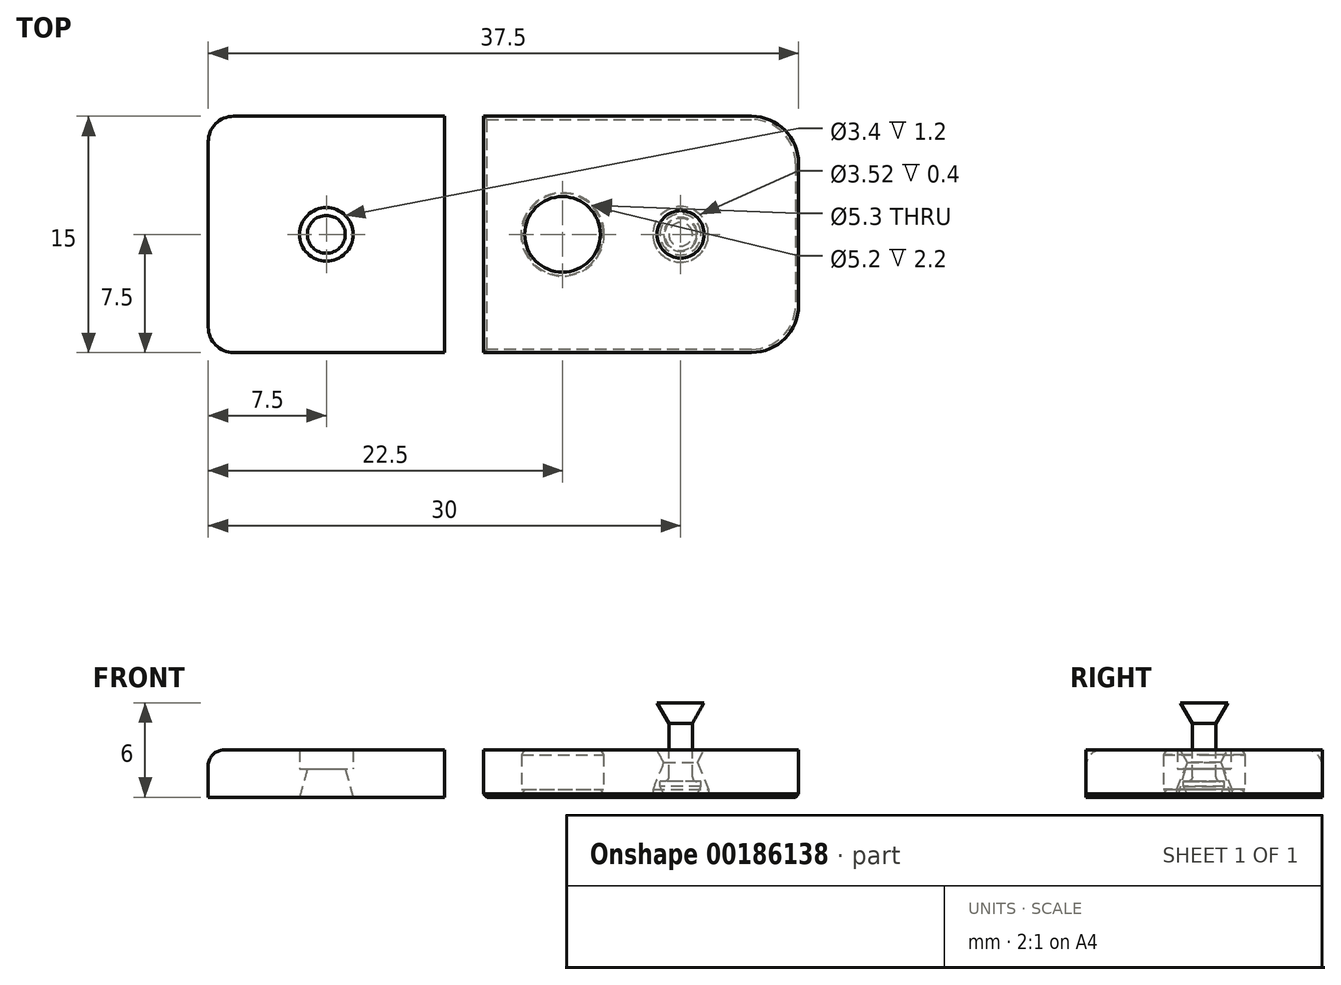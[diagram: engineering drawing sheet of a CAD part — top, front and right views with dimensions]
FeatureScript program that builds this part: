
annotation { "Feature Type Name" : "Feature", "Feature Type Description" : "" }
export const myFeature = defineFeature(function(context is Context, id is Id, definition is map)
    precondition{}
    {
        {
            var Q0;
            Q0=qCreatedBy(makeId("Top.planeOp"),FACE);
            var sketch = newSketch(context, id + "F0", { "sketchPlane" : qUnion([Q0])});
            skLineSegment(sketch, "E0.bottom", {"start": v(-12.5, 7.5) * mm, "end": v(7.5, 7.5) * mm});
            skLineSegment(sketch, "E0.top", {"start": v(-12.5, -7.5) * mm, "end": v(7.5, -7.5) * mm});
            skLineSegment(sketch, "E0.left", {"start": v(-12.5, 7.5) * mm, "end": v(-12.5, -7.5) * mm});
            skLineSegment(sketch, "E0.right", {"start": v(7.5, 7.5) * mm, "end": v(7.5, -7.5) * mm});
            skSolve(sketch);
        }
        {
            var Q0;
            Q0=makeQuery(id+"F0.imprint","IMPRINT",FACE,{"disambiguationData":[TD([[makeQuery(id+"F0.imprint","IMPRINT",EDGE,{"derivedFrom":sQuery(id+"F0.wireOp",EDGE,"E0.bottom")}),-1.0]])]});
            extrude(context, id + "F1", {"entities" : qUnion([Q0]), "depth" : 3 * mm});
        }
        {
            var Q0;
            Q0=qCreatedBy(makeId("Front.planeOp"),FACE);
            var sketch = newSketch(context, id + "F2", { "sketchPlane" : qUnion([Q0])});
            skLineSegment(sketch, "E1", {"start": v(0, 3.74) * mm, "end": v(0, -0.54) * mm, "construction": true});
            skLineSegment(sketch, "E2", {"start": v(-1.76, 0) * mm, "end": v(0, 0) * mm});
            skLineSegment(sketch, "E3", {"start": v(-1.07, 2.2) * mm, "end": v(-1.5, 3) * mm});
            skLineSegment(sketch, "E4", {"start": v(-1.5, 3) * mm, "end": v(0, 3) * mm});
            skLineSegment(sketch, "E5", {"start": v(0, 3) * mm, "end": v(0, 0) * mm});
            skLineSegment(sketch, "E6", {"start": v(-1.76, 0) * mm, "end": v(-1.76, 0.5) * mm});
            skLineSegment(sketch, "E7", {"start": v(-1.76, 0.5) * mm, "end": v(-1.07, 2.2) * mm});
            skSolve(sketch);
        }
        {
            var Q0;
            Q0 = qSketchRegion(id + "F2", true);
            var Q1;
            Q1=sQuery(id+"F2.wireOp",EDGE,"E1");
            revolve(context, id + "F3", {"operationType" : NewBodyOperationType.REMOVE, "entities" : qUnion([Q0]), "axis" : qUnion([Q1]), "revolveType" : RevolveType.FULL, "oppositeDirection" : true});
        }
        {
            var Q0;
            Q0=qCreatedBy(makeId("Front.planeOp"),FACE);
            var sketch = newSketch(context, id + "F4", { "sketchPlane" : qUnion([Q0])});
            skLineSegment(sketch, "E8", {"start": v(0, 6) * mm, "end": v(-1.5, 6) * mm});
            skLineSegment(sketch, "E9", {"start": v(-1.5, 6) * mm, "end": v(-0.75, 4.7) * mm});
            skLineSegment(sketch, "E10", {"start": v(-1.05, 1) * mm, "end": v(-1.3, 1) * mm});
            skLineSegment(sketch, "E11", {"start": v(-1.3, 1) * mm, "end": v(-1.3, 0.7) * mm});
            skLineSegment(sketch, "E12", {"start": v(-1.3, 0.7) * mm, "end": v(-1.02, 0.1) * mm});
            skLineSegment(sketch, "E13", {"start": v(-1.02, 0.1) * mm, "end": v(-2.5, 0.1) * mm});
            skLineSegment(sketch, "E14", {"start": v(-2.5, 0.1) * mm, "end": v(-2.5, 0) * mm});
            skLineSegment(sketch, "E15", {"start": v(-2.5, 0) * mm, "end": v(0, 0) * mm});
            skLineSegment(sketch, "E16", {"start": v(0, 7.34) * mm, "end": v(0, -1.08) * mm, "construction": true});
            skLineSegment(sketch, "E17", {"start": v(-0.75, 4.7) * mm, "end": v(-0.75, 1.3) * mm});
            skPoint(sketch, "E18.visualSharp", {"position": v(-0.75, 1) * mm});
            skArc(sketch, "E18.filletArc", {"start": v(-1.05, 1) * mm, "mid": v(-0.84, 1.09) * mm, "end": v(-0.75, 1.3) * mm});
            skLineSegment(sketch, "E19", {"start": v(0, 6) * mm, "end": v(0, 0) * mm});
            skSolve(sketch);
        }
        {
            var Q0;
            Q0=makeQuery(id+"F4.imprint","IMPRINT",FACE,{"disambiguationData":[TD([[makeQuery(id+"F4.imprint","IMPRINT",EDGE,{"derivedFrom":sQuery(id+"F4.wireOp",EDGE,"E8")}),1.0]])]});
            var Q1;
            Q1=sQuery(id+"F4.wireOp",EDGE,"E16");
            revolve(context, id + "F5", {"operationType" : NewBodyOperationType.ADD, "entities" : qUnion([Q0]), "axis" : qUnion([Q1]), "revolveType" : RevolveType.FULL});
        }
        {
            var Q0;
            Q0=qCreatedBy(makeId("Top.planeOp"),FACE);
            var sketch = newSketch(context, id + "F6", { "sketchPlane" : qUnion([Q0])});
            skLineSegment(sketch, "E20.bottom", {"start": v(-30, 7.5) * mm, "end": v(-15, 7.5) * mm});
            skLineSegment(sketch, "E20.top", {"start": v(-30, -7.5) * mm, "end": v(-15, -7.5) * mm});
            skLineSegment(sketch, "E20.left", {"start": v(-30, 7.5) * mm, "end": v(-30, -7.5) * mm});
            skLineSegment(sketch, "E20.right", {"start": v(-15, 7.5) * mm, "end": v(-15, -7.5) * mm});
            skSolve(sketch);
        }
        {
            var Q0;
            Q0=makeQuery(id+"F6.imprint","IMPRINT",FACE,{"disambiguationData":[TD([[makeQuery(id+"F6.imprint","IMPRINT",EDGE,{"derivedFrom":sQuery(id+"F6.wireOp",EDGE,"E20.bottom")}),-1.0]])]});
            extrude(context, id + "F7", {"entities" : qUnion([Q0]), "depth" : 3 * mm});
        }
        {
            var Q0;
            Q0=qCreatedBy(makeId("Front.planeOp"),FACE);
            var sketch = newSketch(context, id + "F8", { "sketchPlane" : qUnion([Q0])});
            skLineSegment(sketch, "E21", {"start": v(-22.5, 6.48) * mm, "end": v(-22.5, -5.25) * mm, "construction": true});
            skLineSegment(sketch, "E22", {"start": v(-22.5, 3) * mm, "end": v(-24.2, 3) * mm});
            skLineSegment(sketch, "E23", {"start": v(-24.2, 3) * mm, "end": v(-24.2, 1.8) * mm});
            skLineSegment(sketch, "E24", {"start": v(-24.2, 1.8) * mm, "end": v(-23.7, 1.8) * mm});
            skLineSegment(sketch, "E25", {"start": v(-23.7, 1.8) * mm, "end": v(-24.2, 0) * mm});
            skLineSegment(sketch, "E26", {"start": v(-24.2, 0) * mm, "end": v(-22.5, 0) * mm});
            skLineSegment(sketch, "E27", {"start": v(-22.5, 0) * mm, "end": v(-22.5, 3) * mm});
            skSolve(sketch);
        }
        {
            var Q0;
            Q0 = qSketchRegion(id + "F8", true);
            var Q1;
            Q1=sQuery(id+"F8.wireOp",EDGE,"E21");
            revolve(context, id + "F9", {"operationType" : NewBodyOperationType.REMOVE, "entities" : qUnion([Q0]), "axis" : qUnion([Q1]), "revolveType" : RevolveType.FULL, "oppositeDirection" : true});
        }
        {
            var Q0;
            Q0=makeQuery(id+"F1.opExtrude","SWEPT_EDGE",EDGE,{"disambiguationData":[OSD([sQuery(id+"F0.wireOp",EDGE,"E0.top"),sQuery(id+"F0.wireOp",EDGE,"E0.right")])]});
            var Q1;
            Q1=makeQuery(id+"F1.opExtrude","SWEPT_EDGE",EDGE,{"disambiguationData":[OSD([sQuery(id+"F0.wireOp",EDGE,"E0.bottom"),sQuery(id+"F0.wireOp",EDGE,"E0.right")])]});
            fillet(context, id + "F10", {"entities" : qUnion([Q0, Q1]), "radius" : 3 * mm, "tangentPropagation" : true, "allowEdgeOverflow" : false});
        }
        {
            var Q0;
            Q0=makeQuery(id+"F1.opExtrude","CAP_EDGE",EDGE,{"disambiguationData":[OSD([sQuery(id+"F0.wireOp",EDGE,"E0.right")])],"isStart":true});
            var Q1;
            Q1=makeQuery(id+"F1.opExtrude","CAP_EDGE",EDGE,{"disambiguationData":[OSD([sQuery(id+"F0.wireOp",EDGE,"E0.top")])],"isStart":true});
            var Q2;
            Q2=makeQuery(id+"F1.opExtrude","CAP_EDGE",EDGE,{"disambiguationData":[OSD([sQuery(id+"F0.wireOp",EDGE,"E0.left")])],"isStart":true});
            var Q3;
            Q3=makeQuery(id+"F1.opExtrude","CAP_EDGE",EDGE,{"disambiguationData":[OSD([sQuery(id+"F0.wireOp",EDGE,"E0.bottom")])],"isStart":true});
            chamfer(context, id + "F11", {"entities" : qUnion([Q0, Q1, Q2, Q3]), "width" : .2 * mm, "tangentPropagation" : true});
        }
        {
            var Q0;
            Q0=makeQuery(id+"F7.opExtrude","SWEPT_EDGE",EDGE,{"disambiguationData":[OSD([sQuery(id+"F6.wireOp",EDGE,"E20.top"),sQuery(id+"F6.wireOp",EDGE,"E20.left")])]});
            var Q1;
            Q1=makeQuery(id+"F7.opExtrude","SWEPT_EDGE",EDGE,{"disambiguationData":[OSD([sQuery(id+"F6.wireOp",EDGE,"E20.bottom"),sQuery(id+"F6.wireOp",EDGE,"E20.left")])]});
            fillet(context, id + "F12", {"entities" : qUnion([Q0, Q1]), "radius" : 1.6 * mm, "tangentPropagation" : true, "allowEdgeOverflow" : false});
        }
        {
            var Q0;
            Q0=makeQuery(id+"F7.opExtrude","CAP_EDGE",EDGE,{"disambiguationData":[OSD([sQuery(id+"F6.wireOp",EDGE,"E20.top")])],"isStart":false});
            fillet(context, id + "F13", {"entities" : qUnion([Q0]), "radius" : 1 * mm, "tangentPropagation" : true, "allowEdgeOverflow" : false});
        }
        {
            var Q0;
            Q0=qCreatedBy(makeId("Front.planeOp"),FACE);
            var sketch = newSketch(context, id + "F14", { "sketchPlane" : qUnion([Q0])});
            skLineSegment(sketch, "E28", {"start": v(-7.5, 3) * mm, "end": v(-7.5, -2.51) * mm, "construction": true});
            skLineSegment(sketch, "E29", {"start": v(-10.1, 0.5) * mm, "end": v(-9.9, 0.5) * mm});
            skLineSegment(sketch, "E30", {"start": v(-10.15, 0) * mm, "end": v(-7.5, 0) * mm});
            skLineSegment(sketch, "E31", {"start": v(-7.5, 0) * mm, "end": v(-7.5, 3) * mm});
            skLineSegment(sketch, "E32", {"start": v(-9.9, 0.5) * mm, "end": v(-10.15, 0.1) * mm});
            skLineSegment(sketch, "E33", {"start": v(-10.15, 0.1) * mm, "end": v(-10.15, 0) * mm});
            skLineSegment(sketch, "E34", {"start": v(-10.1, 2.7) * mm, "end": v(-9.9, 3) * mm});
            skLineSegment(sketch, "E35", {"start": v(-7.5, 3) * mm, "end": v(-9.9, 3) * mm});
            skLineSegment(sketch, "E36", {"start": v(-10.1, 2.7) * mm, "end": v(-10.1, 0.5) * mm});
            skSolve(sketch);
        }
        {
            var Q0;
            Q0 = qSketchRegion(id + "F14", true);
            var Q1;
            Q1=sQuery(id+"F14.wireOp",EDGE,"E28");
            revolve(context, id + "F15", {"operationType" : NewBodyOperationType.REMOVE, "entities" : qUnion([Q0]), "axis" : qUnion([Q1]), "revolveType" : RevolveType.FULL, "oppositeDirection" : true});
        }
    });
